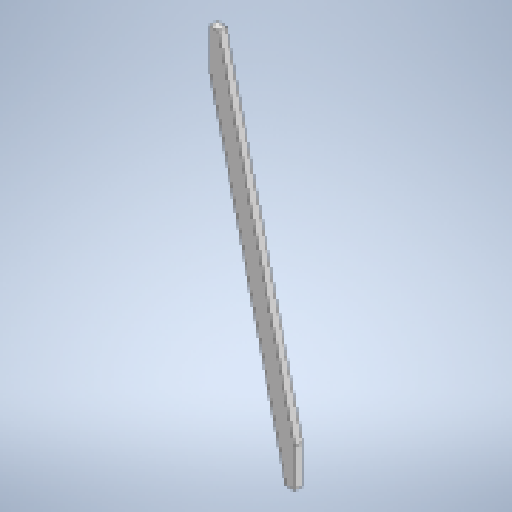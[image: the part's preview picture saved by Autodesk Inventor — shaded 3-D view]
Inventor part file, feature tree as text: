
AUTODESK INVENTOR PART (.ipt)
format: ipt  version: 2025.1 (Build 291241020, 241B)  size: 141,824 bytes
history: native  units: in
note: dims shown in document units (in); Inventor stores cm internally (conversion verified against a paired STEP export)
features: other x8, reference x6, extrude x1, sketch x1
ambient origin geometry x8: Origin, YZ Plane, XZ Plane, XY Plane, X Axis, Y Axis, Z Axis, Center Point
bodies: Solid1 (feature_tree)
feature tree (16):
  extrude  "Extrusion1"  [1 undecoded]
  sketch  "Sketch1"  dims[d4=1.5in d5=0.0in]
  reference  "Reference1"
  reference  "Reference2"
  reference  "Reference3"
  reference  "Reference4"
  reference  "Reference5"
  reference  "Reference6"
  other  "<userpath>\Documents\Tburn24\Assembly1.iam"
  other  "Assembly1.iam"
  other  "7'5x2x4:1"
  other  "6'x4x4:12"
  other  "7'5x4x4:1"
  other  "6'x4x4:14"
  other  "6'x4x4:1"
  other  "6'x4x4:23"
note: 1 required parameter value undecoded (feature->parameter linkage not recoverable at this tier; creation-order binding heuristic only, values carry confidence <= 0.55)
